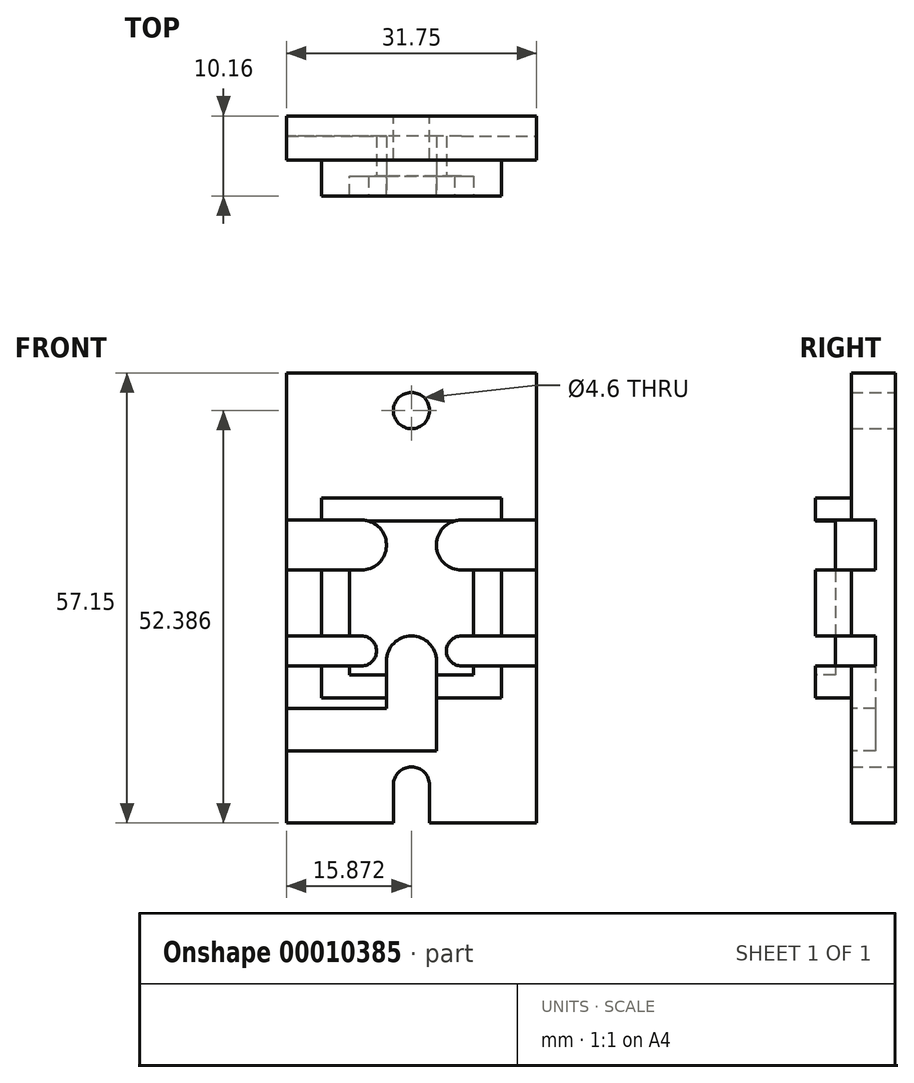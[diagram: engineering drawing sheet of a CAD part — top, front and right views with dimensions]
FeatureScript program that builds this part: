
annotation { "Feature Type Name" : "Feature", "Feature Type Description" : "" }
export const myFeature = defineFeature(function(context is Context, id is Id, definition is map)
    precondition{}
    {
        {
            var Q0;
            Q0=qCreatedBy(makeId("Front.planeOp"),FACE);
            var sketch = newSketch(context, id + "F0", { "sketchPlane" : qUnion([Q0])});
            skLineSegment(sketch, "E0.bottom", {"start": v(-22.73, 23.87) * mm, "end": v(9.02, 23.87) * mm});
            skLineSegment(sketch, "E0.top", {"start": v(-22.73, -33.28) * mm, "end": v(-9.16, -33.28) * mm});
            skLineSegment(sketch, "E0.left", {"start": v(-22.73, 23.87) * mm, "end": v(-22.73, -33.28) * mm});
            skLineSegment(sketch, "E0.right", {"start": v(9.02, 23.87) * mm, "end": v(9.02, -33.28) * mm});
            skCircle(sketch, "E1", {"center": v(-6.86, 19.1) * mm, "radius": 2.3 * mm});
            skArc(sketch, "E2", {"start": v(-4.56, -28.47) * mm, "mid": v(-6.86, -26.17) * mm, "end": v(-9.16, -28.47) * mm});
            skLineSegment(sketch, "E3", {"start": v(-9.16, -28.47) * mm, "end": v(-9.16, -33.28) * mm});
            skLineSegment(sketch, "E4", {"start": v(-4.56, -28.47) * mm, "end": v(-4.56, -33.28) * mm});
            skLineSegment(sketch, "E5.trimOffspring", {"start": v(-4.56, -33.28) * mm, "end": v(9.02, -33.28) * mm});
            skSolve(sketch);
        }
        {
            var Q0;
            Q0 = qSketchRegion(id + "F0", true);
            extrude(context, id + "F1", {"entities" : qUnion([Q0]), "depth" : 5.6 * mm});
        }
        {
            var Q0;
            Q0=makeQuery(id+"F1.opExtrude","CAP_FACE",FACE,{"disambiguationData":[OSD([sQuery(id+"F0.wireOp",EDGE,"E0.bottom"),sQuery(id+"F0.wireOp",EDGE,"E0.top"),sQuery(id+"F0.wireOp",EDGE,"E0.left"),sQuery(id+"F0.wireOp",EDGE,"E0.right"),sQuery(id+"F0.wireOp",EDGE,"E1"),sQuery(id+"F0.wireOp",EDGE,"E2"),sQuery(id+"F0.wireOp",EDGE,"E3"),sQuery(id+"F0.wireOp",EDGE,"E4"),sQuery(id+"F0.wireOp",EDGE,"E5.trimOffspring")])],"isStart":false});
            var sketch = newSketch(context, id + "F2", { "sketchPlane" : qUnion([Q0])});
            skLineSegment(sketch, "E6.bottom", {"start": v(-18.29, 8) * mm, "end": v(4.57, 8) * mm});
            skLineSegment(sketch, "E6.top", {"start": v(-18.29, -17.4) * mm, "end": v(4.57, -17.4) * mm});
            skLineSegment(sketch, "E6.left", {"start": v(-18.29, 8) * mm, "end": v(-18.29, -17.4) * mm});
            skLineSegment(sketch, "E6.right", {"start": v(4.57, 8) * mm, "end": v(4.57, -17.4) * mm});
            skSolve(sketch);
        }
        {
            var Q0;
            Q0 = qSketchRegion(id + "F2", true);
            extrude(context, id + "F3", {"entities" : qUnion([Q0]), "operationType" : NewBodyOperationType.ADD, "depth" : 4.57 * mm});
        }
        {
            var Q0;
            Q0=makeQuery(id+"F3.opExtrude","CAP_FACE",FACE,{"disambiguationData":[OSD([sQuery(id+"F2.wireOp",EDGE,"E6.bottom"),sQuery(id+"F2.wireOp",EDGE,"E6.top"),sQuery(id+"F2.wireOp",EDGE,"E6.left"),sQuery(id+"F2.wireOp",EDGE,"E6.right")])],"isStart":false});
            var sketch = newSketch(context, id + "F4", { "sketchPlane" : qUnion([Q0])});
            skLineSegment(sketch, "E7.bottom", {"start": v(-14.73, 5.07) * mm, "end": v(1.02, 5.07) * mm});
            skLineSegment(sketch, "E7.top", {"start": v(-14.73, -14.49) * mm, "end": v(1.02, -14.49) * mm});
            skLineSegment(sketch, "E7.left", {"start": v(-14.73, 5.07) * mm, "end": v(-14.73, -14.49) * mm});
            skLineSegment(sketch, "E7.right", {"start": v(1.02, 5.07) * mm, "end": v(1.02, -14.49) * mm});
            skSolve(sketch);
        }
        {
            var Q0;
            Q0 = qSketchRegion(id + "F4", true);
            extrude(context, id + "F5", {"entities" : qUnion([Q0]), "operationType" : NewBodyOperationType.REMOVE, "oppositeDirection" : true, "depth" : 2.54 * mm});
        }
        {
            var Q0;
            Q0=makeQuery(id+"F3.opExtrude","CAP_FACE",FACE,{"disambiguationData":[OSD([sQuery(id+"F2.wireOp",EDGE,"E6.bottom"),sQuery(id+"F2.wireOp",EDGE,"E6.top"),sQuery(id+"F2.wireOp",EDGE,"E6.left"),sQuery(id+"F2.wireOp",EDGE,"E6.right")])],"isStart":false});
            var sketch = newSketch(context, id + "F6", { "sketchPlane" : qUnion([Q0])});
            skArc(sketch, "E8", {"start": v(-3.68, -12.7) * mm, "mid": v(-6.86, -9.53) * mm, "end": v(-10.03, -12.7) * mm});
            skArc(sketch, "E9", {"start": v(-0.5, -9.53) * mm, "mid": v(-2.41, -11.44) * mm, "end": v(-0.5, -13.34) * mm});
            skArc(sketch, "E10", {"start": v(-13.2, -13.34) * mm, "mid": v(-11.3, -11.44) * mm, "end": v(-13.2, -9.53) * mm});
            skArc(sketch, "E11", {"start": v(-13.2, -1.15) * mm, "mid": v(-10.03, 2.02) * mm, "end": v(-13.2, 5.2) * mm});
            skArc(sketch, "E12", {"start": v(-0.5, 5.2) * mm, "mid": v(-3.68, 2.02) * mm, "end": v(-0.5, -1.15) * mm});
            skLineSegment(sketch, "E13", {"start": v(-13.2, 5.2) * mm, "end": v(-23.3, 5.2) * mm});
            skLineSegment(sketch, "E14", {"start": v(-23.3, 5.2) * mm, "end": v(-23.3, -1.15) * mm});
            skLineSegment(sketch, "E15", {"start": v(-23.3, -1.15) * mm, "end": v(-13.2, -1.15) * mm});
            skLineSegment(sketch, "E16.bottom", {"start": v(-0.5, -9.53) * mm, "end": v(14.32, -9.53) * mm});
            skLineSegment(sketch, "E16.top", {"start": v(-0.5, -13.34) * mm, "end": v(14.32, -13.34) * mm});
            skLineSegment(sketch, "E16.right", {"start": v(14.32, -9.53) * mm, "end": v(14.32, -13.34) * mm});
            skLineSegment(sketch, "E17.bottom", {"start": v(-13.2, -9.53) * mm, "end": v(-28.9, -9.53) * mm});
            skLineSegment(sketch, "E17.top", {"start": v(-13.2, -13.34) * mm, "end": v(-28.9, -13.34) * mm});
            skLineSegment(sketch, "E17.right", {"start": v(-28.9, -9.53) * mm, "end": v(-28.9, -13.34) * mm});
            skPoint(sketch, "E18.right.end.orphan", {"position": v(7.38, -1.15) * mm});
            skLineSegment(sketch, "E19.bottom", {"start": v(-0.5, 5.2) * mm, "end": v(12.3, 5.2) * mm});
            skLineSegment(sketch, "E19.top", {"start": v(-0.5, -1.15) * mm, "end": v(12.3, -1.15) * mm});
            skLineSegment(sketch, "E19.right", {"start": v(12.3, 5.2) * mm, "end": v(12.3, -1.15) * mm});
            skPoint(sketch, "E20.right.end.orphan", {"position": v(-3.68, -28.8) * mm});
            skLineSegment(sketch, "E21.top", {"start": v(-3.68, -24.14) * mm, "end": v(-10.03, -24.14) * mm});
            skLineSegment(sketch, "E21.left", {"start": v(-3.68, -12.7) * mm, "end": v(-3.68, -24.14) * mm});
            skLineSegment(sketch, "E21.right", {"start": v(-10.03, -12.7) * mm, "end": v(-10.03, -18.76) * mm});
            skLineSegment(sketch, "E22.bottom", {"start": v(-3.68, -24.14) * mm, "end": v(-24.89, -24.14) * mm});
            skLineSegment(sketch, "E22.top", {"start": v(-10.03, -18.76) * mm, "end": v(-24.89, -18.76) * mm});
            skLineSegment(sketch, "E22.left", {"start": v(-3.68, -24.14) * mm, "end": v(-3.68, -18.76) * mm});
            skLineSegment(sketch, "E22.right", {"start": v(-24.89, -24.14) * mm, "end": v(-24.89, -18.76) * mm});
            skSolve(sketch);
        }
        {
            var Q0;
            Q0 = qSketchRegion(id + "F6", true);
            extrude(context, id + "F7", {"entities" : qUnion([Q0]), "operationType" : NewBodyOperationType.REMOVE, "oppositeDirection" : true, "depth" : 7.62 * mm});
        }
    });
